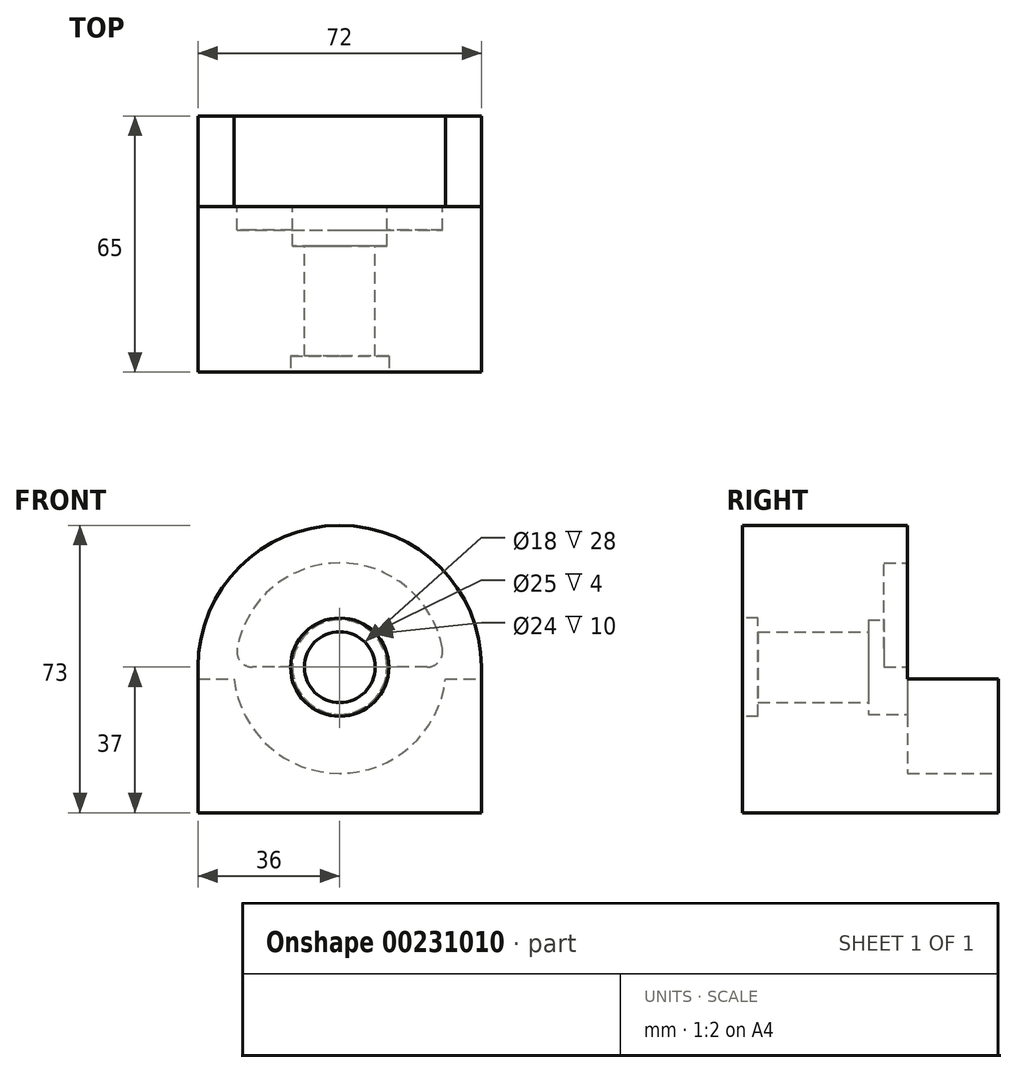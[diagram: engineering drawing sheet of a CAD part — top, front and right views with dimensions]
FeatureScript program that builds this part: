
annotation { "Feature Type Name" : "Feature", "Feature Type Description" : "" }
export const myFeature = defineFeature(function(context is Context, id is Id, definition is map)
    precondition{}
    {
        {
            var Q0;
            Q0=qCreatedBy(makeId("Front.planeOp"),FACE);
            var sketch = newSketch(context, id + "F0", { "sketchPlane" : qUnion([Q0])});
            skCircle(sketch, "E0", {"center": v(0, 0) * mm, "radius": 9 * mm});
            skCircle(sketch, "E1", {"center": v(0, 0) * mm, "radius": 36 * mm});
            skLineSegment(sketch, "E2.bottom", {"start": v(-36, 0) * mm, "end": v(36, 0) * mm});
            skLineSegment(sketch, "E2.top", {"start": v(-36, -37) * mm, "end": v(36, -37) * mm});
            skLineSegment(sketch, "E2.left", {"start": v(-36, 0) * mm, "end": v(-36, -37) * mm});
            skLineSegment(sketch, "E2.right", {"start": v(36, 0) * mm, "end": v(36, -37) * mm});
            skSolve(sketch);
        }
        {
            var Q0;
            {var subQ0=sQuery(id+"F0.wireOp",EDGE,"E2.bottom");var subQ1=sQuery(id+"F0.wireOp",EDGE,"E0");var subQ2=makeQuery(id+"F0.imprint","INTERSECT",VERTEX,{"disambiguationData":[OD(0.0)],"derivedFrom":[subQ1,subQ0]});Q0=makeQuery(id+"F0.imprint","IMPRINT",FACE,{"disambiguationData":[TD([[makeQuery(id+"F0.imprint","IMPRINT",EDGE,{"disambiguationData":[TD([[subQ2,1.0]])],"derivedFrom":subQ1}),-1.0]])]});}
            var Q1;
            {var subQ0=sQuery(id+"F0.wireOp",EDGE,"E2.bottom");var subQ1=sQuery(id+"F0.wireOp",EDGE,"E0");var subQ2=makeQuery(id+"F0.imprint","INTERSECT",VERTEX,{"disambiguationData":[OD(0.0)],"derivedFrom":[subQ1,subQ0]});Q1=makeQuery(id+"F0.imprint","IMPRINT",FACE,{"disambiguationData":[TD([[makeQuery(id+"F0.imprint","IMPRINT",EDGE,{"disambiguationData":[TD([[subQ2,-1.0]])],"derivedFrom":subQ1}),-1.0]])]});}
            var Q2;
            Q2=makeQuery(id+"F0.imprint","IMPRINT",FACE,{"disambiguationData":[TD([[makeQuery(id+"F0.imprint","IMPRINT",EDGE,{"derivedFrom":sQuery(id+"F0.wireOp",EDGE,"E2.top")}),1.0]])]});
            extrude(context, id + "F1", {"entities" : qUnion([Q0, Q1, Q2]), "depth" : 65 * mm});
        }
        {
            var Q0;
            Q0=makeQuery(id+"F1.opExtrude","CAP_FACE",FACE,{"disambiguationData":[OSD([sQuery(id+"F0.wireOp",EDGE,"E0"),sQuery(id+"F0.wireOp",EDGE,"E1"),sQuery(id+"F0.wireOp",EDGE,"E2.top"),sQuery(id+"F0.wireOp",EDGE,"E2.left"),sQuery(id+"F0.wireOp",EDGE,"E2.right")])],"isStart":false});
            var sketch = newSketch(context, id + "F2", { "sketchPlane" : qUnion([Q0])});
            skCircle(sketch, "E3", {"center": v(0, 0) * mm, "radius": 12.5 * mm});
            skSolve(sketch);
        }
        {
            var Q0;
            Q0=makeQuery(id+"F2.imprint","IMPRINT",FACE,{"disambiguationData":[TD([[makeQuery(id+"F2.imprint","IMPRINT",EDGE,{"derivedFrom":sQuery(id+"F2.wireOp",EDGE,"E3")}),1.0]])]});
            extrude(context, id + "F3", {"entities" : qUnion([Q0]), "operationType" : NewBodyOperationType.REMOVE, "oppositeDirection" : true, "depth" : 4 * mm});
        }
        {
            var Q0;
            Q0=makeQuery(id+"F1.opExtrude","SWEPT_FACE",FACE,{"disambiguationData":[OSD([sQuery(id+"F0.wireOp",EDGE,"E2.right")])]});
            var sketch = newSketch(context, id + "F4", { "sketchPlane" : qUnion([Q0])});
            skLineSegment(sketch, "E4", {"start": v(0, -37) * mm, "end": v(0, -3) * mm});
            skLineSegment(sketch, "E5", {"start": v(0, -3) * mm, "end": v(-23, -3) * mm});
            skLineSegment(sketch, "E6", {"start": v(-23, -3) * mm, "end": v(-23, 42) * mm});
            skLineSegment(sketch, "E7", {"start": v(-65, 0) * mm, "end": v(-65, 40) * mm});
            skLineSegment(sketch, "E8", {"start": v(-65, 40) * mm, "end": v(0, 40) * mm});
            skLineSegment(sketch, "E9", {"start": v(0, 40) * mm, "end": v(0, -3) * mm});
            skSolve(sketch);
        }
        {
            var Q0;
            {var subQ0=sQuery(id+"F4.wireOp",EDGE,"E8");var subQ5=sQuery(id+"F4.wireOp",EDGE,"E9");var subQ7=makeQuery(id+"F4.imprint","INTERSECT",VERTEX,{"derivedFrom":[subQ0,subQ5]});Q0=makeQuery(id+"F4.imprint","IMPRINT",FACE,{"disambiguationData":[TD([[makeQuery(id+"F4.imprint","IMPRINT",EDGE,{"disambiguationData":[TD([[subQ7,1.0]])],"derivedFrom":subQ0}),-1.0]])]});}
            var Q1;
            {var subQ0=sQuery(id+"F4.wireOp",EDGE,"E5");Q1=makeQuery(id+"F4.imprint","IMPRINT",FACE,{"disambiguationData":[TD([[makeQuery(id+"F4.imprint","IMPRINT",EDGE,{"derivedFrom":subQ0}),-1.0]])]});}
            extrude(context, id + "F5", {"entities" : qUnion([Q0, Q1]), "operationType" : NewBodyOperationType.REMOVE, "oppositeDirection" : true, "depth" : 72 * mm});
        }
        {
            var Q0;
            Q0=makeQuery(id+"F1.opExtrude","CAP_FACE",FACE,{"disambiguationData":[OSD([sQuery(id+"F0.wireOp",EDGE,"E0"),sQuery(id+"F0.wireOp",EDGE,"E1"),sQuery(id+"F0.wireOp",EDGE,"E2.top"),sQuery(id+"F0.wireOp",EDGE,"E2.left"),sQuery(id+"F0.wireOp",EDGE,"E2.right")])],"isStart":true});
            var sketch = newSketch(context, id + "F6", { "sketchPlane" : qUnion([Q0])});
            skCircle(sketch, "E10", {"center": v(0, 0) * mm, "radius": 27 * mm});
            skSolve(sketch);
        }
        {
            var Q0;
            {var subQ1=sQuery(id+"F0.wireOp",EDGE,"E0");var subQ13=makeQuery(id+"F1.opExtrude","CAP_EDGE",EDGE,{"disambiguationData":[OSD([subQ1])],"isStart":true});Q0=makeQuery(id+"F6.imprint","IMPRINT",FACE,{"disambiguationData":[TD([[makeQuery(id+"F6.imprint","IMPRINT",EDGE,{"derivedFrom":subQ13}),-1.0]])]});}
            var Q1;
            {var subQ1=sQuery(id+"F0.wireOp",EDGE,"E0");var subQ13=makeQuery(id+"F1.opExtrude","CAP_EDGE",EDGE,{"disambiguationData":[OSD([subQ1])],"isStart":true});Q1=makeQuery(id+"F6.imprint","IMPRINT",FACE,{"disambiguationData":[TD([[makeQuery(id+"F6.imprint","IMPRINT",EDGE,{"derivedFrom":subQ13}),1.0]])]});}
            extrude(context, id + "F7", {"entities" : qUnion([Q0, Q1]), "operationType" : NewBodyOperationType.REMOVE, "oppositeDirection" : true, "depth" : 23 * mm});
        }
        {
            var Q0;
            Q0=makeQuery(id+"F7.boolean.opBoolean","MERGE",FACE,{"derivedFrom":[makeQuery(id+"F5.boolean.opBoolean","COPY",FACE,{"derivedFrom":makeQuery(id+"F5.opExtrude","SWEPT_FACE",FACE,{"disambiguationData":[OSD([sQuery(id+"F4.wireOp",EDGE,"E6")])]})}),makeQuery(id+"F7.opExtrude","CAP_FACE",FACE,{"disambiguationData":[OSD([sQuery(id+"F6.wireOp",EDGE,"E10")])],"isStart":false})]});
            var sketch = newSketch(context, id + "F8", { "sketchPlane" : qUnion([Q0])});
            skCircle(sketch, "E11", {"center": v(0, 0) * mm, "radius": 12 * mm});
            skSolve(sketch);
        }
        {
            var Q0;
            Q0=makeQuery(id+"F8.imprint","IMPRINT",FACE,{"disambiguationData":[TD([[makeQuery(id+"F8.imprint","IMPRINT",EDGE,{"derivedFrom":sQuery(id+"F8.wireOp",EDGE,"E11")}),1.0]])]});
            extrude(context, id + "F9", {"entities" : qUnion([Q0]), "operationType" : NewBodyOperationType.REMOVE, "oppositeDirection" : true, "depth" : 10 * mm});
        }
        {
            var Q0;
            Q0=makeQuery(id+"F7.boolean.opBoolean","MERGE",FACE,{"derivedFrom":[makeQuery(id+"F5.boolean.opBoolean","COPY",FACE,{"derivedFrom":makeQuery(id+"F5.opExtrude","SWEPT_FACE",FACE,{"disambiguationData":[OSD([sQuery(id+"F4.wireOp",EDGE,"E6")])]})}),makeQuery(id+"F7.opExtrude","CAP_FACE",FACE,{"disambiguationData":[OSD([sQuery(id+"F6.wireOp",EDGE,"E10")])],"isStart":false})]});
            var sketch = newSketch(context, id + "F10", { "sketchPlane" : qUnion([Q0])});
            skArc(sketch, "E12", {"start": v(26.08, 4.71) * mm, "mid": v(0, 26.5) * mm, "end": v(-26.08, 4.71) * mm});
            skLineSegment(sketch, "E13", {"start": v(-22.14, 0) * mm, "end": v(22.14, 0) * mm});
            skPoint(sketch, "E14.visualSharp", {"position": v(-26.5, 0) * mm});
            skArc(sketch, "E14.filletArc", {"start": v(-26.08, 4.71) * mm, "mid": v(-25.21, 1.44) * mm, "end": v(-22.14, 0) * mm});
            skPoint(sketch, "E15.visualSharp", {"position": v(26.5, 0) * mm});
            skArc(sketch, "E15.filletArc", {"start": v(22.14, 0) * mm, "mid": v(25.21, 1.44) * mm, "end": v(26.08, 4.71) * mm});
            skSolve(sketch);
        }
        {
            var Q0;
            Q0=makeQuery(id+"F10.imprint","IMPRINT",FACE,{"disambiguationData":[TD([[makeQuery(id+"F10.imprint","IMPRINT",EDGE,{"derivedFrom":sQuery(id+"F10.wireOp",EDGE,"E12")}),1.0]])]});
            extrude(context, id + "F11", {"entities" : qUnion([Q0]), "operationType" : NewBodyOperationType.REMOVE, "oppositeDirection" : true, "depth" : 6 * mm});
        }
    });
